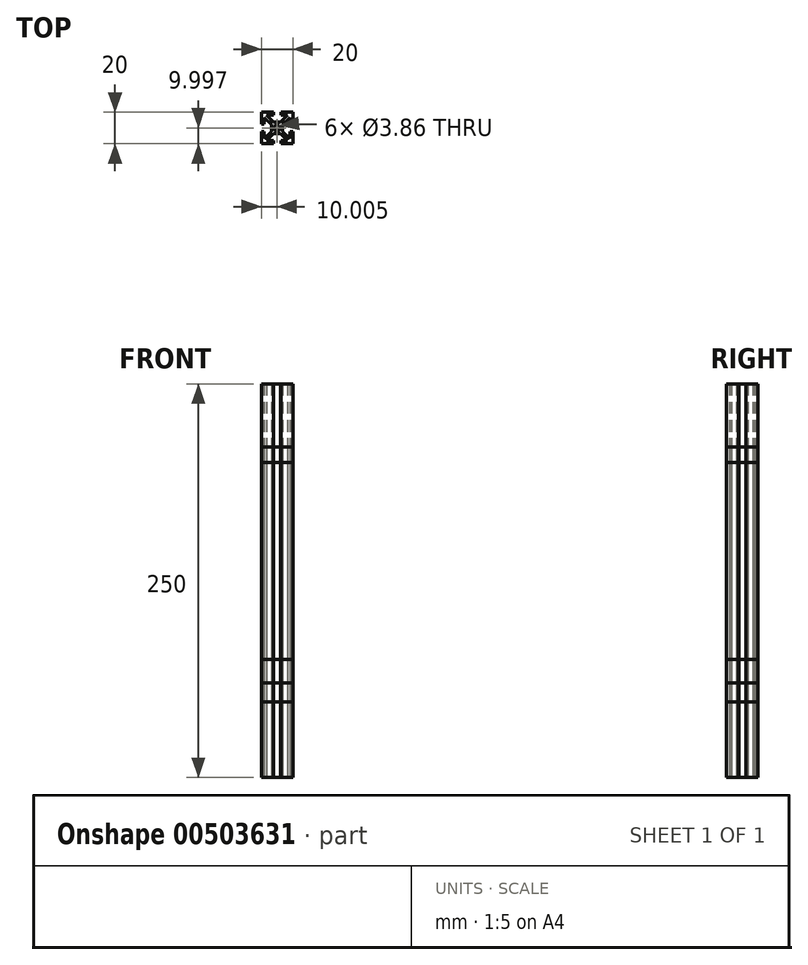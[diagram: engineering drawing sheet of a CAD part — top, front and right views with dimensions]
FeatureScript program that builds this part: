
annotation { "Feature Type Name" : "Feature", "Feature Type Description" : "" }
export const myFeature = defineFeature(function(context is Context, id is Id, definition is map)
    precondition{}
    {
        {
            var Q0;
            Q0=qCreatedBy(makeId("Top.planeOp"),FACE);
            var sketch = newSketch(context, id + "F0", { "sketchPlane" : qUnion([Q0])});
            skFitSpline(sketch, "E0.0", {"points": [v(5.81, 15) * mm, v(8.35, 15) * mm, v(10.9, 15) * mm, v(13.43, 15) * mm]});
            skFitSpline(sketch, "E0.1", {"points": [v(5.81, 7.38) * mm, v(5.81, 9.92) * mm, v(5.81, 12.46) * mm, v(5.81, 15) * mm]});
            skFitSpline(sketch, "E0.2", {"points": [v(7.7, 7.38) * mm, v(7.7, 8.83) * mm, v(7.7, 10.28) * mm, v(7.7, 11.73) * mm]});
            skFitSpline(sketch, "E0.3", {"points": [v(12.2, 7.23) * mm, v(10.7, 8.73) * mm, v(9.2, 10.23) * mm, v(7.7, 11.73) * mm]});
            skFitSpline(sketch, "E0.4", {"points": [v(9.1, 13.12) * mm, v(10.6, 11.62) * mm, v(12.1, 10.11) * mm, v(13.61, 8.6) * mm]});
            skFitSpline(sketch, "E0.5", {"points": [v(9.1, 13.12) * mm, v(10.54, 13.12) * mm, v(11.99, 13.12) * mm, v(13.43, 13.12) * mm]});
            skFitSpline(sketch, "E0.6", {"points": [v(13.43, 15) * mm, v(13.43, 14.37) * mm, v(13.43, 13.75) * mm, v(13.43, 13.12) * mm]});
            skFitSpline(sketch, "E0.7", {"points": [v(7.7, 7.38) * mm, v(7.07, 7.38) * mm, v(6.44, 7.38) * mm, v(5.81, 7.38) * mm]});
            skFitSpline(sketch, "E0.8", {"points": [v(5.81, 2.61) * mm, v(6.44, 2.61) * mm, v(7.07, 2.61) * mm, v(7.7, 2.61) * mm]});
            skFitSpline(sketch, "E0.9", {"points": [v(7.7, 2.61) * mm, v(7.7, 1.16) * mm, v(7.7, -0.29) * mm, v(7.7, -1.74) * mm]});
            skFitSpline(sketch, "E0.10", {"points": [v(7.7, -1.74) * mm, v(9.2, -0.24) * mm, v(10.7, 1.26) * mm, v(12.2, 2.76) * mm]});
            skFitSpline(sketch, "E0.11", {"points": [v(12.2, 7.23) * mm, v(12.2, 5.74) * mm, v(12.2, 4.25) * mm, v(12.2, 2.76) * mm]});
            skFitSpline(sketch, "E0.12", {"points": [v(13.61, 8.6) * mm, v(15.08, 8.6) * mm, v(16.55, 8.6) * mm, v(18.02, 8.6) * mm]});
            skFitSpline(sketch, "E0.13", {"points": [v(18.02, 8.6) * mm, v(19.53, 10.11) * mm, v(21.03, 11.62) * mm, v(22.54, 13.12) * mm]});
            skFitSpline(sketch, "E0.14", {"points": [v(22.54, 13.12) * mm, v(21.1, 13.12) * mm, v(19.64, 13.12) * mm, v(18.2, 13.12) * mm]});
            skFitSpline(sketch, "E0.15", {"points": [v(18.2, 13.12) * mm, v(18.2, 13.75) * mm, v(18.2, 14.37) * mm, v(18.2, 15) * mm]});
            skFitSpline(sketch, "E0.16", {"points": [v(18.2, 15) * mm, v(20.73, 15) * mm, v(23.27, 15) * mm, v(25.81, 15) * mm]});
            skFitSpline(sketch, "E0.17", {"points": [v(25.81, 15) * mm, v(25.81, 12.46) * mm, v(25.81, 9.92) * mm, v(25.81, 7.38) * mm]});
            skFitSpline(sketch, "E0.18", {"points": [v(25.81, 7.38) * mm, v(25.18, 7.38) * mm, v(24.55, 7.38) * mm, v(23.92, 7.38) * mm]});
            skFitSpline(sketch, "E0.19", {"points": [v(23.92, 11.73) * mm, v(23.92, 10.28) * mm, v(23.92, 8.83) * mm, v(23.92, 7.38) * mm]});
            skFitSpline(sketch, "E0.20", {"points": [v(23.92, 11.73) * mm, v(22.42, 10.23) * mm, v(20.92, 8.73) * mm, v(19.42, 7.23) * mm]});
            skFitSpline(sketch, "E0.21", {"points": [v(19.42, 2.76) * mm, v(19.42, 4.25) * mm, v(19.42, 5.74) * mm, v(19.42, 7.23) * mm]});
            skFitSpline(sketch, "E0.22", {"points": [v(19.42, 2.76) * mm, v(20.92, 1.26) * mm, v(22.42, -0.24) * mm, v(23.92, -1.74) * mm]});
            skFitSpline(sketch, "E0.23", {"points": [v(23.92, -1.74) * mm, v(23.92, -0.29) * mm, v(23.92, 1.16) * mm, v(23.92, 2.61) * mm]});
            skFitSpline(sketch, "E0.24", {"points": [v(23.92, 2.61) * mm, v(24.55, 2.61) * mm, v(25.18, 2.61) * mm, v(25.81, 2.61) * mm]});
            skFitSpline(sketch, "E0.25", {"points": [v(25.81, 2.61) * mm, v(25.81, 0.07) * mm, v(25.81, -2.46) * mm, v(25.81, -5) * mm]});
            skFitSpline(sketch, "E0.26", {"points": [v(18.2, -3.13) * mm, v(19.64, -3.13) * mm, v(21.08, -3.13) * mm, v(22.53, -3.13) * mm]});
            skFitSpline(sketch, "E0.27", {"points": [v(22.53, -3.13) * mm, v(21.03, -1.63) * mm, v(19.52, -0.12) * mm, v(18.01, 1.39) * mm]});
            skPoint(sketch, "E0.28", {"position": v(17.6, 4.24) * mm});
            skFitSpline(sketch, "E0.29", {"points": [v(18.01, 1.39) * mm, v(16.54, 1.39) * mm, v(15.07, 1.39) * mm, v(13.6, 1.39) * mm]});
            skFitSpline(sketch, "E0.30", {"points": [v(13.6, 1.39) * mm, v(12.1, -0.12) * mm, v(10.6, -1.63) * mm, v(9.09, -3.13) * mm]});
            skFitSpline(sketch, "E0.31", {"points": [v(13.43, -3.13) * mm, v(11.98, -3.13) * mm, v(10.53, -3.13) * mm, v(9.09, -3.13) * mm]});
            skFitSpline(sketch, "E0.32", {"points": [v(13.43, -3.13) * mm, v(13.43, -3.76) * mm, v(13.43, -4.38) * mm, v(13.43, -5) * mm]});
            skFitSpline(sketch, "E0.33", {"points": [v(13.43, -5) * mm, v(10.89, -5) * mm, v(8.35, -5) * mm, v(5.81, -5) * mm]});
            skFitSpline(sketch, "E0.34", {"points": [v(5.81, -5) * mm, v(5.81, -2.46) * mm, v(5.81, 0.07) * mm, v(5.81, 2.61) * mm]});
            skFitSpline(sketch, "E0.35", {"points": [v(25.81, -5) * mm, v(23.27, -5) * mm, v(20.73, -5) * mm, v(18.2, -5) * mm]});
            skFitSpline(sketch, "E0.36", {"points": [v(18.2, -5) * mm, v(18.2, -4.38) * mm, v(18.2, -3.76) * mm, v(18.2, -3.13) * mm]});
            skSolve(sketch);
        }
        {
            var Q0;
            Q0=qCreatedBy(makeId("Top.planeOp"),FACE);
            var sketch = newSketch(context, id + "F1", { "sketchPlane" : qUnion([Q0])});
            skPoint(sketch, "E1.0", {"position": v(18.2, 15) * mm});
            skPoint(sketch, "E1.1", {"position": v(18.2, 13.12) * mm});
            skPoint(sketch, "E1.2", {"position": v(25.81, 15) * mm});
            skPoint(sketch, "E1.3", {"position": v(25.81, 7.38) * mm});
            skPoint(sketch, "E1.4", {"position": v(23.92, 7.38) * mm});
            skPoint(sketch, "E1.5", {"position": v(23.92, 11.73) * mm});
            skPoint(sketch, "E1.6", {"position": v(22.54, 13.12) * mm});
            skPoint(sketch, "E1.7", {"position": v(18.02, 8.6) * mm});
            skPoint(sketch, "E1.8", {"position": v(13.61, 8.6) * mm});
            skPoint(sketch, "E1.9", {"position": v(19.42, 7.23) * mm});
            skPoint(sketch, "E1.10", {"position": v(19.42, 2.76) * mm});
            skPoint(sketch, "E1.11", {"position": v(9.1, 13.12) * mm});
            skPoint(sketch, "E1.12", {"position": v(7.7, 11.73) * mm});
            skPoint(sketch, "E1.13", {"position": v(7.7, 7.38) * mm});
            skPoint(sketch, "E1.14", {"position": v(5.81, 7.38) * mm});
            skPoint(sketch, "E1.15", {"position": v(5.81, 15) * mm});
            skPoint(sketch, "E1.16", {"position": v(13.43, 15) * mm});
            skPoint(sketch, "E1.17", {"position": v(13.43, 13.12) * mm});
            skPoint(sketch, "E1.18", {"position": v(12.2, 7.23) * mm});
            skPoint(sketch, "E1.19", {"position": v(12.2, 2.76) * mm});
            skPoint(sketch, "E1.20", {"position": v(7.7, -1.74) * mm});
            skPoint(sketch, "E1.21", {"position": v(7.7, 2.61) * mm});
            skPoint(sketch, "E1.22", {"position": v(5.81, 2.61) * mm});
            skPoint(sketch, "E1.23", {"position": v(5.81, -5) * mm});
            skPoint(sketch, "E1.24", {"position": v(13.43, -5) * mm});
            skPoint(sketch, "E1.25", {"position": v(13.43, -3.13) * mm});
            skPoint(sketch, "E1.26", {"position": v(9.09, -3.13) * mm});
            skPoint(sketch, "E1.27", {"position": v(13.6, 1.39) * mm});
            skPoint(sketch, "E1.28", {"position": v(18.01, 1.39) * mm});
            skPoint(sketch, "E1.29", {"position": v(22.53, -3.13) * mm});
            skPoint(sketch, "E1.30", {"position": v(18.2, -3.13) * mm});
            skPoint(sketch, "E1.31", {"position": v(18.2, -5) * mm});
            skPoint(sketch, "E1.32", {"position": v(25.81, -5) * mm});
            skPoint(sketch, "E1.33", {"position": v(25.81, 2.61) * mm});
            skPoint(sketch, "E1.34", {"position": v(23.92, 2.61) * mm});
            skPoint(sketch, "E1.35", {"position": v(23.92, -1.74) * mm});
            skLineSegment(sketch, "E2", {"start": v(5.81, 15) * mm, "end": v(13.43, 15) * mm});
            skLineSegment(sketch, "E3", {"start": v(13.43, 15) * mm, "end": v(13.43, 13.12) * mm});
            skLineSegment(sketch, "E4", {"start": v(13.43, 13.12) * mm, "end": v(9.1, 13.12) * mm});
            skLineSegment(sketch, "E5", {"start": v(9.1, 13.12) * mm, "end": v(13.61, 8.6) * mm});
            skLineSegment(sketch, "E6", {"start": v(13.61, 8.6) * mm, "end": v(18.02, 8.6) * mm});
            skLineSegment(sketch, "E7", {"start": v(18.02, 8.6) * mm, "end": v(22.54, 13.12) * mm});
            skLineSegment(sketch, "E8", {"start": v(18.2, 13.12) * mm, "end": v(22.54, 13.12) * mm});
            skLineSegment(sketch, "E9", {"start": v(18.2, 13.12) * mm, "end": v(18.2, 15) * mm});
            skLineSegment(sketch, "E10", {"start": v(18.2, 15) * mm, "end": v(25.81, 15) * mm});
            skLineSegment(sketch, "E11", {"start": v(25.81, 15) * mm, "end": v(25.81, 7.38) * mm});
            skLineSegment(sketch, "E12", {"start": v(25.81, 7.38) * mm, "end": v(23.92, 7.38) * mm});
            skLineSegment(sketch, "E13", {"start": v(23.92, 7.38) * mm, "end": v(23.92, 11.73) * mm});
            skLineSegment(sketch, "E14", {"start": v(23.92, 11.73) * mm, "end": v(19.42, 7.23) * mm});
            skLineSegment(sketch, "E15", {"start": v(19.42, 7.23) * mm, "end": v(19.42, 2.76) * mm});
            skLineSegment(sketch, "E16", {"start": v(19.42, 2.76) * mm, "end": v(23.92, -1.74) * mm});
            skLineSegment(sketch, "E17", {"start": v(23.92, -1.74) * mm, "end": v(23.92, 2.61) * mm});
            skLineSegment(sketch, "E18", {"start": v(23.92, 2.61) * mm, "end": v(25.81, 2.61) * mm});
            skLineSegment(sketch, "E19", {"start": v(25.81, 2.61) * mm, "end": v(25.81, -5) * mm});
            skLineSegment(sketch, "E20", {"start": v(25.81, -5) * mm, "end": v(18.2, -5) * mm});
            skLineSegment(sketch, "E21", {"start": v(18.2, -5) * mm, "end": v(18.2, -3.13) * mm});
            skLineSegment(sketch, "E22", {"start": v(18.2, -3.13) * mm, "end": v(22.53, -3.13) * mm});
            skLineSegment(sketch, "E23", {"start": v(22.53, -3.13) * mm, "end": v(18.01, 1.39) * mm});
            skLineSegment(sketch, "E24", {"start": v(18.01, 1.39) * mm, "end": v(13.6, 1.39) * mm});
            skLineSegment(sketch, "E25", {"start": v(13.6, 1.39) * mm, "end": v(9.09, -3.13) * mm});
            skLineSegment(sketch, "E26", {"start": v(9.09, -3.13) * mm, "end": v(13.43, -3.13) * mm});
            skLineSegment(sketch, "E27", {"start": v(13.43, -3.13) * mm, "end": v(13.43, -5) * mm});
            skLineSegment(sketch, "E28", {"start": v(13.43, -5) * mm, "end": v(5.81, -5) * mm});
            skLineSegment(sketch, "E29", {"start": v(5.81, -5) * mm, "end": v(5.81, 2.61) * mm});
            skLineSegment(sketch, "E30", {"start": v(5.81, 2.61) * mm, "end": v(7.7, 2.61) * mm});
            skLineSegment(sketch, "E31", {"start": v(7.7, 2.61) * mm, "end": v(7.7, -1.74) * mm});
            skLineSegment(sketch, "E32", {"start": v(7.7, -1.74) * mm, "end": v(12.2, 2.76) * mm});
            skLineSegment(sketch, "E33", {"start": v(12.2, 2.76) * mm, "end": v(12.2, 7.23) * mm});
            skLineSegment(sketch, "E34", {"start": v(12.2, 7.23) * mm, "end": v(7.7, 11.73) * mm});
            skLineSegment(sketch, "E35", {"start": v(7.7, 11.73) * mm, "end": v(7.7, 7.38) * mm});
            skLineSegment(sketch, "E36", {"start": v(7.7, 7.38) * mm, "end": v(5.81, 7.38) * mm});
            skLineSegment(sketch, "E37", {"start": v(5.81, 7.38) * mm, "end": v(5.81, 15) * mm});
            skPoint(sketch, "E38.centerSnap0", {"position": v(15.82, 8.6) * mm});
            skPoint(sketch, "E38.centerSnap1", {"position": v(12.2, 5) * mm});
            skPoint(sketch, "E39.0", {"position": v(17.6, 4.24) * mm});
            skCircle(sketch, "E40", {"center": v(15.82, 5) * mm, "radius": 1.93 * mm});
            skSolve(sketch);
        }
        {
            var Q0;
            Q0=makeQuery(id+"F1.imprint","IMPRINT",FACE,{"disambiguationData":[TD([[makeQuery(id+"F1.imprint","IMPRINT",EDGE,{"derivedFrom":sQuery(id+"F1.wireOp",EDGE,"E2")}),-1.0]])]});
            extrude(context, id + "F2", {"entities" : qUnion([Q0]), "depth" : 250 * mm});
        }
        {
            var Q0;
            Q0=makeQuery(id+"F1.imprint","IMPRINT",FACE,{"disambiguationData":[TD([[makeQuery(id+"F1.imprint","IMPRINT",EDGE,{"derivedFrom":sQuery(id+"F1.wireOp",EDGE,"E2")}),-1.0]])]});
            extrude(context, id + "F3", {"entities" : qUnion([Q0]), "depth" : 60 * mm});
        }
        {
            var Q0;
            Q0=makeQuery(id+"F1.imprint","IMPRINT",FACE,{"disambiguationData":[TD([[makeQuery(id+"F1.imprint","IMPRINT",EDGE,{"derivedFrom":sQuery(id+"F1.wireOp",EDGE,"E2")}),-1.0]])]});
            extrude(context, id + "F4", {"entities" : qUnion([Q0]), "offsetDistance" : 25 * mm, "depth" : 75 * mm});
        }
        {
            var Q0;
            Q0=makeQuery(id+"F1.imprint","IMPRINT",FACE,{"disambiguationData":[TD([[makeQuery(id+"F1.imprint","IMPRINT",EDGE,{"derivedFrom":sQuery(id+"F1.wireOp",EDGE,"E2")}),-1.0]])]});
            extrude(context, id + "F5", {"entities" : qUnion([Q0]), "depth" : 200 * mm, "offsetDistance" : 25 * mm});
        }
        {
            var Q0;
            Q0=makeQuery(id+"F1.imprint","IMPRINT",FACE,{"disambiguationData":[TD([[makeQuery(id+"F1.imprint","IMPRINT",EDGE,{"derivedFrom":sQuery(id+"F1.wireOp",EDGE,"E2")}),-1.0]])]});
            extrude(context, id + "F6", {"entities" : qUnion([Q0]), "depth" : 48 * mm, "offsetDistance" : 25 * mm});
        }
        {
            var Q0;
            Q0=makeQuery(id+"F1.imprint","IMPRINT",FACE,{"disambiguationData":[TD([[makeQuery(id+"F1.imprint","IMPRINT",EDGE,{"derivedFrom":sQuery(id+"F1.wireOp",EDGE,"E2")}),-1.0]])]});
            extrude(context, id + "F7", {"entities" : qUnion([Q0]), "depth" : 210 * mm, "offsetDistance" : 25 * mm});
        }
    });
